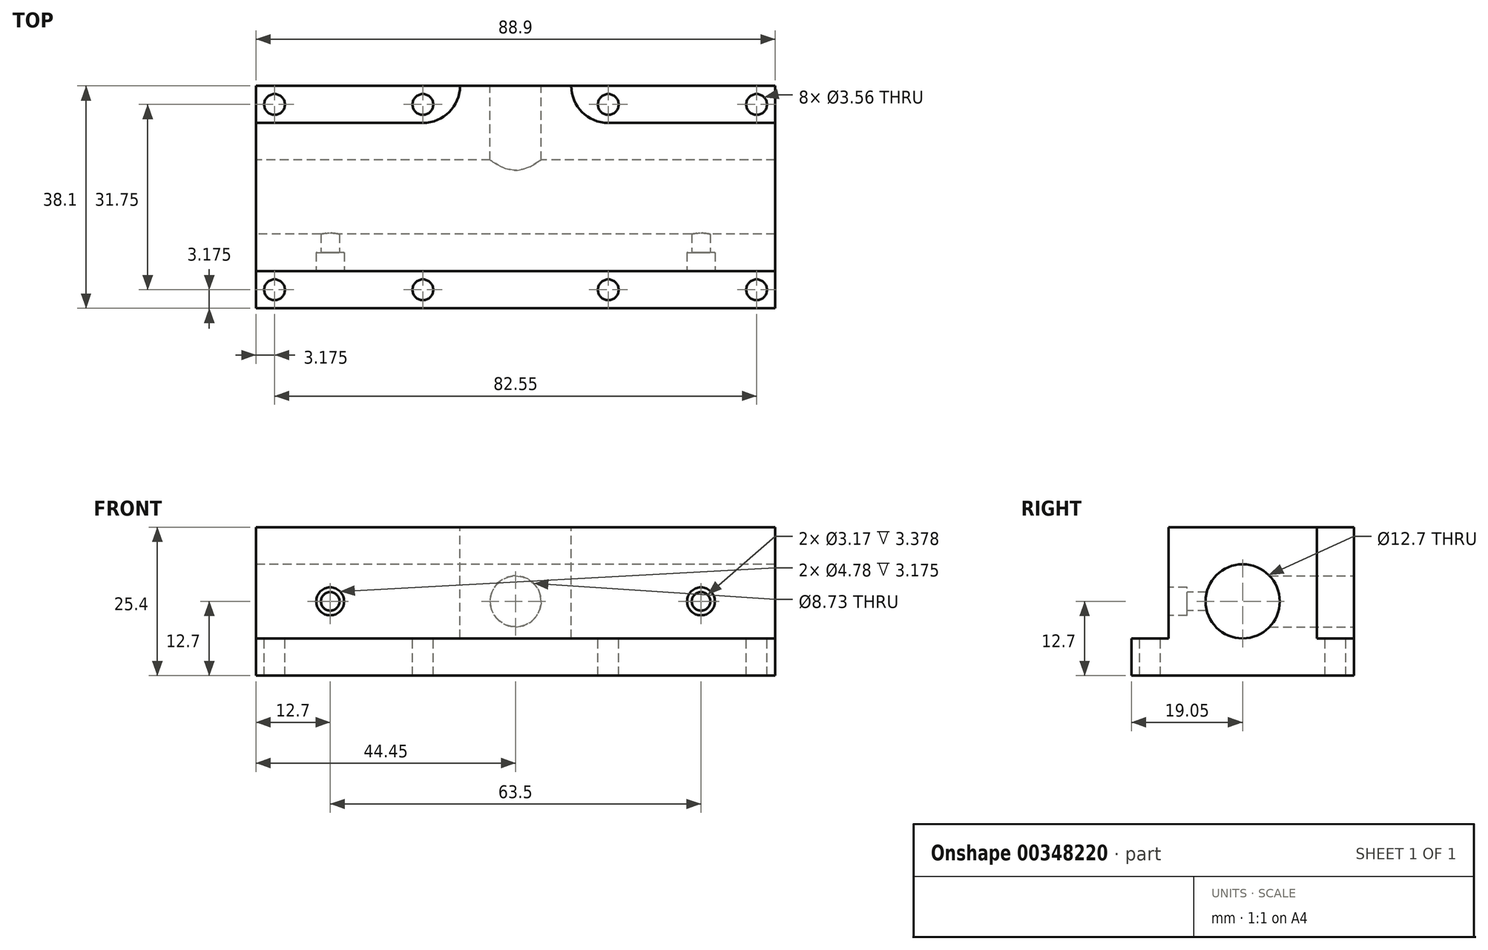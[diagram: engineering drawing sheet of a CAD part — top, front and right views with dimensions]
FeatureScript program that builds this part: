
annotation { "Feature Type Name" : "Feature", "Feature Type Description" : "" }
export const myFeature = defineFeature(function(context is Context, id is Id, definition is map)
    precondition{}
    {
        {
            var Q0;
            Q0=qCreatedBy(makeId("Right.planeOp"),FACE);
            var sketch = newSketch(context, id + "F0", { "sketchPlane" : qUnion([Q0])});
            skLineSegment(sketch, "E0.bottom", {"start": v(-19.05, -12.7) * mm, "end": v(19.05, -12.7) * mm});
            skLineSegment(sketch, "E0.top", {"start": v(-19.05, 12.7) * mm, "end": v(19.05, 12.7) * mm});
            skLineSegment(sketch, "E0.left", {"start": v(-19.05, -12.7) * mm, "end": v(-19.05, 12.7) * mm});
            skLineSegment(sketch, "E0.right", {"start": v(19.05, -12.7) * mm, "end": v(19.05, 12.7) * mm});
            skPoint(sketch, "E1", {"position": v(0, 12.7) * mm});
            skPoint(sketch, "E2", {"position": v(19.05, 0) * mm});
            skCircle(sketch, "E3", {"center": v(0, 0) * mm, "radius": 6.35 * mm});
            skSolve(sketch);
        }
        {
            var Q0;
            Q0=qSketchRegion(id+"F0",true);
            extrude(context, id + "F1", {"entities" : qUnion([Q0]), "endBound" : BoundingType.SYMMETRIC, "depth" : 88.9 * mm});
        }
        {
            var Q0;
            Q0=makeQuery(id+"F1.opExtrude","SWEPT_FACE",FACE,{"disambiguationData":[OSD([sQuery(id+"F0.wireOp",EDGE,"E0.top")])]});
            var sketch = newSketch(context, id + "F2", { "sketchPlane" : qUnion([Q0])});
            skLineSegment(sketch, "E4.bottom", {"start": v(-44.45, 19.05) * mm, "end": v(-9.53, 19.05) * mm});
            skLineSegment(sketch, "E4.top", {"start": v(-44.45, 12.7) * mm, "end": v(-15.87, 12.7) * mm});
            skLineSegment(sketch, "E4.left", {"start": v(-44.45, 19.05) * mm, "end": v(-44.45, 12.7) * mm});
            skLineSegment(sketch, "E4.right", {"start": v(44.45, 19.05) * mm, "end": v(44.45, 12.7) * mm});
            skLineSegment(sketch, "E5.bottom", {"start": v(-44.45, -19.05) * mm, "end": v(44.45, -19.05) * mm});
            skLineSegment(sketch, "E5.top", {"start": v(-44.45, -12.7) * mm, "end": v(44.45, -12.7) * mm});
            skLineSegment(sketch, "E5.left", {"start": v(-44.45, -19.05) * mm, "end": v(-44.45, -12.7) * mm});
            skLineSegment(sketch, "E5.right", {"start": v(44.45, -19.05) * mm, "end": v(44.45, -12.7) * mm});
            skLineSegment(sketch, "E6.trimOffspring", {"start": v(15.87, 12.7) * mm, "end": v(44.45, 12.7) * mm});
            skLineSegment(sketch, "E7.trimOffspring", {"start": v(9.52, 19.05) * mm, "end": v(44.45, 19.05) * mm});
            skArc(sketch, "E8", {"start": v(-9.52, 19.05) * mm, "mid": v(-11.38, 14.56) * mm, "end": v(-15.87, 12.7) * mm});
            skArc(sketch, "E9", {"start": v(9.52, 19.05) * mm, "mid": v(11.38, 14.56) * mm, "end": v(15.87, 12.7) * mm});
            skSolve(sketch);
        }
        {
            var Q0;
            Q0=qSketchRegion(id+"F2",true);
            extrude(context, id + "F3", {"entities" : qUnion([Q0]), "operationType" : NewBodyOperationType.REMOVE, "oppositeDirection" : true, "depth" : 19.05 * mm});
        }
        {
            var Q0;
            Q0=makeQuery(id+"F1.opExtrude","SWEPT_FACE",FACE,{"disambiguationData":[OSD([sQuery(id+"F0.wireOp",EDGE,"E0.right")])]});
            var sketch = newSketch(context, id + "F4", { "sketchPlane" : qUnion([Q0])});
            skPoint(sketch, "E10", {"position": v(0, 0) * mm});
            skSolve(sketch);
        }
        {
            var Q0;
            Q0=sQuery(id+"F4.wireOp",VERTEX,"E10");
            var Q1;
            Q1=makeQuery(id+"F1.opExtrude","SWEPT_BODY",BODY,{"disambiguationData":[OSD([sQuery(id+"F0.wireOp",EDGE,"E0.bottom"),sQuery(id+"F0.wireOp",EDGE,"E0.top"),sQuery(id+"F0.wireOp",EDGE,"E0.left"),sQuery(id+"F0.wireOp",EDGE,"E0.right"),sQuery(id+"F0.wireOp",EDGE,"E3")])]});
            hole(context, id + "F5", {"style" : HoleStyle.SIMPLE, "holeDiameter" : 8.73 * mm, "endStyle" : HoleEndStyle.BLIND, "holeDepth" : 19.05 * mm, "locations" : qUnion([Q0]), "scope" : qUnion([Q1])});
        }
        {
            var Q0;
            Q0=makeQuery(id+"F3.boolean.opBoolean","COPY",FACE,{"derivedFrom":makeQuery(id+"F3.opExtrude","SWEPT_FACE",FACE,{"disambiguationData":[OSD([sQuery(id+"F2.wireOp",EDGE,"E5.top")])]})});
            var sketch = newSketch(context, id + "F6", { "sketchPlane" : qUnion([Q0])});
            skPoint(sketch, "E11", {"position": v(-31.75, 0) * mm});
            skPoint(sketch, "E12", {"position": v(31.75, 0) * mm});
            skSolve(sketch);
        }
        {
            var Q0;
            Q0=sQuery(id+"F6.wireOp",VERTEX,"E11");
            var Q1;
            Q1=sQuery(id+"F6.wireOp",VERTEX,"E12");
            var Q2;
            Q2=makeQuery(id+"F1.opExtrude","SWEPT_BODY",BODY,{"disambiguationData":[OSD([sQuery(id+"F0.wireOp",EDGE,"E0.bottom"),sQuery(id+"F0.wireOp",EDGE,"E0.top"),sQuery(id+"F0.wireOp",EDGE,"E0.left"),sQuery(id+"F0.wireOp",EDGE,"E0.right"),sQuery(id+"F0.wireOp",EDGE,"E3")])]});
            hole(context, id + "F7", {"style" : HoleStyle.C_BORE, "holeDiameter" : 3.17 * mm, "cBoreDiameter" : 4.78 * mm, "cBoreDepth" : 3.17 * mm, "endStyle" : HoleEndStyle.BLIND, "holeDepth" : 12.7 * mm, "locations" : qUnion([Q0, Q1]), "scope" : qUnion([Q2])});
        }
        {
            var Q0;
            Q0=makeQuery(id+"F3.boolean.opBoolean","COPY",FACE,{"derivedFrom":makeQuery(id+"F3.opExtrude","CAP_FACE",FACE,{"disambiguationData":[OSD([sQuery(id+"F2.wireOp",EDGE,"E5.bottom"),sQuery(id+"F2.wireOp",EDGE,"E5.top"),sQuery(id+"F2.wireOp",EDGE,"E5.left"),sQuery(id+"F2.wireOp",EDGE,"E5.right")])],"isStart":false})});
            var sketch = newSketch(context, id + "F8", { "sketchPlane" : qUnion([Q0])});
            skPoint(sketch, "E13", {"position": v(-41.28, 15.88) * mm});
            skPoint(sketch, "E14", {"position": v(-15.88, 15.88) * mm});
            skPoint(sketch, "E15", {"position": v(15.87, 15.88) * mm});
            skPoint(sketch, "E16", {"position": v(41.27, 15.88) * mm});
            skPoint(sketch, "E17", {"position": v(-41.28, -15.88) * mm});
            skPoint(sketch, "E18", {"position": v(-15.88, -15.88) * mm});
            skPoint(sketch, "E19", {"position": v(15.87, -15.88) * mm});
            skPoint(sketch, "E20", {"position": v(41.27, -15.88) * mm});
            skSolve(sketch);
        }
        {
            var Q0;
            Q0=sQuery(id+"F8.wireOp",VERTEX,"E13");
            var Q1;
            Q1=sQuery(id+"F8.wireOp",VERTEX,"E14");
            var Q2;
            Q2=sQuery(id+"F8.wireOp",VERTEX,"E15");
            var Q3;
            Q3=sQuery(id+"F8.wireOp",VERTEX,"E16");
            var Q4;
            Q4=sQuery(id+"F8.wireOp",VERTEX,"E20");
            var Q5;
            Q5=sQuery(id+"F8.wireOp",VERTEX,"E19");
            var Q6;
            Q6=sQuery(id+"F8.wireOp",VERTEX,"E18");
            var Q7;
            Q7=sQuery(id+"F8.wireOp",VERTEX,"E17");
            var Q8;
            Q8=makeQuery(id+"F1.opExtrude","SWEPT_BODY",BODY,{"disambiguationData":[OSD([sQuery(id+"F0.wireOp",EDGE,"E0.bottom"),sQuery(id+"F0.wireOp",EDGE,"E0.top"),sQuery(id+"F0.wireOp",EDGE,"E0.left"),sQuery(id+"F0.wireOp",EDGE,"E0.right"),sQuery(id+"F0.wireOp",EDGE,"E3")])]});
            hole(context, id + "F9", {"style" : HoleStyle.SIMPLE, "holeDiameter" : 3.56 * mm, "endStyle" : HoleEndStyle.THROUGH, "locations" : qUnion([Q0, Q1, Q2, Q3, Q4, Q5, Q6, Q7]), "scope" : qUnion([Q8])});
        }
    });
